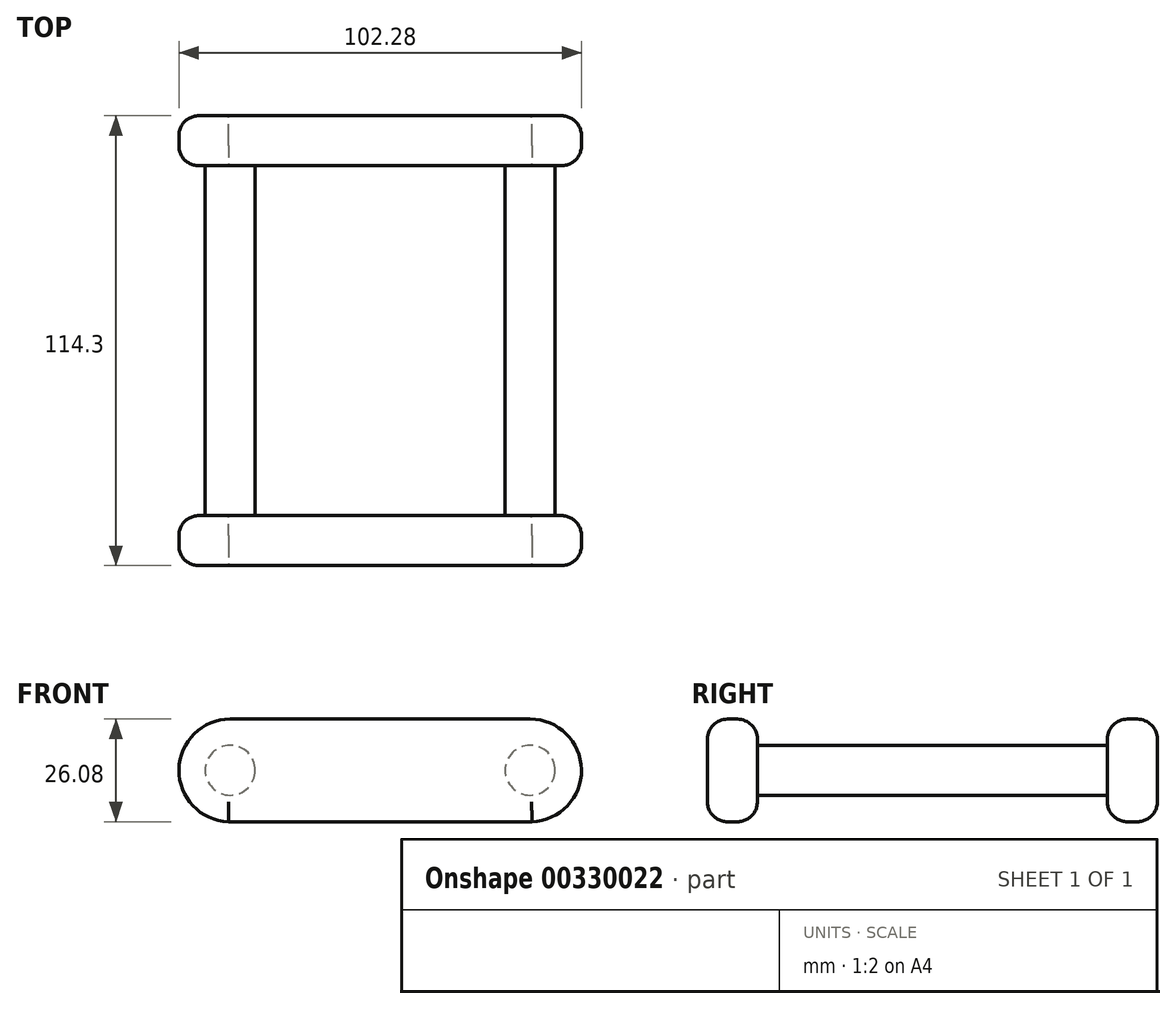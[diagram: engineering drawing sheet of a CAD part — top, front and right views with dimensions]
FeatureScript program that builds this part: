
annotation { "Feature Type Name" : "Feature", "Feature Type Description" : "" }
export const myFeature = defineFeature(function(context is Context, id is Id, definition is map)
    precondition{}
    {
        {
            var Q0;
            Q0=qCreatedBy(makeId("Front.planeOp"),FACE);
            var sketch = newSketch(context, id + "F0", { "sketchPlane" : qUnion([Q0])});
            skCircle(sketch, "E0", {"center": v(-38.1, 0) * mm, "radius": 6.35 * mm});
            skCircle(sketch, "E1", {"center": v(38.1, 0) * mm, "radius": 6.35 * mm});
            skSolve(sketch);
        }
        {
            var Q0;
            Q0 = qSketchRegion(id + "F0", true);
            extrude(context, id + "F1", {"entities" : qUnion([Q0]), "depth" : 50.8 * mm, "hasSecondDirection" : true, "secondDirectionOppositeDirection" : true, "secondDirectionDepth" : 50.8 * mm});
        }
        {
            var Q0;
            Q0=qCreatedBy(makeId("Front.planeOp"),FACE);
            cPlane(context, id + "F2", {"entities" : qUnion([Q0]), "cplaneType" : CPlaneType.OFFSET, "offset" : 50.8 * mm, "width" : 152.4 * mm, "height" : 152.4 * mm});
        }
        {
            var Q0;
            Q0=qCreatedBy(id+"F2.planeOp",FACE);
            var sketch = newSketch(context, id + "F3", { "sketchPlane" : qUnion([Q0])});
            skArc(sketch, "E2", {"start": v(-38.1, 12.99) * mm, "mid": v(-51.14, 0.18) * mm, "end": v(-38.57, -13.09) * mm});
            skLineSegment(sketch, "E3", {"start": v(-38.1, 12.99) * mm, "end": v(0, 12.99) * mm});
            skLineSegment(sketch, "E4", {"start": v(-38.57, -13.09) * mm, "end": v(0, -13.09) * mm});
            skLineSegment(sketch, "E5.MirrorCS", {"start": v(38.1, 12.99) * mm, "end": v(0, 12.99) * mm});
            skLineSegment(sketch, "E6.MirrorCS", {"start": v(38.57, -13.09) * mm, "end": v(0, -13.09) * mm});
            skArc(sketch, "E7.MirrorCS", {"start": v(38.1, 12.99) * mm, "mid": v(51.14, 0.18) * mm, "end": v(38.57, -13.09) * mm});
            skSolve(sketch);
        }
        {
            var Q0;
            Q0=makeQuery(id+"F3.imprint","IMPRINT",FACE,{"disambiguationData":[TD([[makeQuery(id+"F3.imprint","IMPRINT",EDGE,{"derivedFrom":sQuery(id+"F3.wireOp",EDGE,"E2")}),1.0]])]});
            var Q1;
            Q1=sQuery(id+"F3.wireOp",EDGE,"E2");
            var Q2;
            Q2=sQuery(id+"F3.wireOp",EDGE,"E3");
            var Q3;
            Q3=sQuery(id+"F3.wireOp",EDGE,"E4");
            var Q4;
            Q4=sQuery(id+"F3.wireOp",EDGE,"E5.MirrorCS");
            var Q5;
            Q5=sQuery(id+"F3.wireOp",EDGE,"E6.MirrorCS");
            var Q6;
            Q6=sQuery(id+"F3.wireOp",EDGE,"E7.MirrorCS");
            extrude(context, id + "F4", {"entities" : qUnion([Q0]), "operationType" : NewBodyOperationType.ADD, "surfaceEntities" : qUnion([Q1, Q2, Q3, Q4, Q5, Q6]), "oppositeDirection" : true, "depth" : 6.35 * mm, "hasSecondDirection" : true, "secondDirectionOppositeDirection" : false, "secondDirectionDepth" : 6.35 * mm});
        }
        {
            var Q0;
            Q0=qCreatedBy(makeId("Front.planeOp"),FACE);
            cPlane(context, id + "F5", {"entities" : qUnion([Q0]), "cplaneType" : CPlaneType.OFFSET, "offset" : 50.8 * mm, "oppositeDirection" : true, "width" : 152.4 * mm, "height" : 152.4 * mm});
        }
        {
            var Q0;
            Q0=qCreatedBy(id+"F5.planeOp",FACE);
            var sketch = newSketch(context, id + "F6", { "sketchPlane" : qUnion([Q0])});
            skArc(sketch, "E8", {"start": v(-38.1, 12.99) * mm, "mid": v(-51.14, 0.18) * mm, "end": v(-38.57, -13.09) * mm});
            skLineSegment(sketch, "E9", {"start": v(-38.1, 12.99) * mm, "end": v(0, 12.99) * mm});
            skLineSegment(sketch, "E10", {"start": v(-38.57, -13.09) * mm, "end": v(0, -13.09) * mm});
            skLineSegment(sketch, "E11.MirrorCS", {"start": v(38.1, 12.99) * mm, "end": v(0, 12.99) * mm});
            skLineSegment(sketch, "E12.MirrorCS", {"start": v(38.57, -13.09) * mm, "end": v(0, -13.09) * mm});
            skArc(sketch, "E13.MirrorCS", {"start": v(38.1, 12.99) * mm, "mid": v(51.14, 0.18) * mm, "end": v(38.57, -13.09) * mm});
            skSolve(sketch);
        }
        {
            var Q0;
            Q0=makeQuery(id+"F6.imprint","IMPRINT",FACE,{"disambiguationData":[TD([[makeQuery(id+"F6.imprint","IMPRINT",EDGE,{"derivedFrom":sQuery(id+"F6.wireOp",EDGE,"E8")}),1.0]])]});
            var Q1;
            Q1=sQuery(id+"F6.wireOp",EDGE,"E8");
            var Q2;
            Q2=sQuery(id+"F6.wireOp",EDGE,"E9");
            var Q3;
            Q3=sQuery(id+"F6.wireOp",EDGE,"E10");
            var Q4;
            Q4=sQuery(id+"F6.wireOp",EDGE,"E11.MirrorCS");
            var Q5;
            Q5=sQuery(id+"F6.wireOp",EDGE,"E12.MirrorCS");
            var Q6;
            Q6=sQuery(id+"F6.wireOp",EDGE,"E13.MirrorCS");
            extrude(context, id + "F7", {"entities" : qUnion([Q0]), "operationType" : NewBodyOperationType.ADD, "surfaceEntities" : qUnion([Q1, Q2, Q3, Q4, Q5, Q6]), "depth" : 6.35 * mm, "hasSecondDirection" : true, "secondDirectionOppositeDirection" : true, "secondDirectionDepth" : 6.35 * mm});
        }
        {
            var Q0;
            Q0=makeQuery(id+"F4.opExtrude","CAP_EDGE",EDGE,{"disambiguationData":[OSD([sQuery(id+"F3.wireOp",EDGE,"E3"),sQuery(id+"F3.wireOp",EDGE,"E5.MirrorCS")])],"isStart":false});
            var Q1;
            Q1=makeQuery(id+"F4.opExtrude","CAP_EDGE",EDGE,{"disambiguationData":[OSD([sQuery(id+"F3.wireOp",EDGE,"E3"),sQuery(id+"F3.wireOp",EDGE,"E5.MirrorCS")])],"isStart":true});
            var Q2;
            Q2=makeQuery(id+"F4.opExtrude","CAP_EDGE",EDGE,{"disambiguationData":[OSD([sQuery(id+"F3.wireOp",EDGE,"E7.MirrorCS")])],"isStart":true});
            var Q3;
            Q3=makeQuery(id+"F4.opExtrude","CAP_EDGE",EDGE,{"disambiguationData":[OSD([sQuery(id+"F3.wireOp",EDGE,"E4"),sQuery(id+"F3.wireOp",EDGE,"E6.MirrorCS")])],"isStart":true});
            var Q4;
            Q4=makeQuery(id+"F4.opExtrude","CAP_EDGE",EDGE,{"disambiguationData":[OSD([sQuery(id+"F3.wireOp",EDGE,"E4"),sQuery(id+"F3.wireOp",EDGE,"E6.MirrorCS")])],"isStart":false});
            var Q5;
            Q5=makeQuery(id+"F7.opExtrude","CAP_EDGE",EDGE,{"disambiguationData":[OSD([sQuery(id+"F6.wireOp",EDGE,"E10"),sQuery(id+"F6.wireOp",EDGE,"E12.MirrorCS")])],"isStart":false});
            var Q6;
            Q6=makeQuery(id+"F7.opExtrude","CAP_EDGE",EDGE,{"disambiguationData":[OSD([sQuery(id+"F6.wireOp",EDGE,"E10"),sQuery(id+"F6.wireOp",EDGE,"E12.MirrorCS")])],"isStart":true});
            var Q7;
            Q7=makeQuery(id+"F7.opExtrude","CAP_EDGE",EDGE,{"disambiguationData":[OSD([sQuery(id+"F6.wireOp",EDGE,"E9"),sQuery(id+"F6.wireOp",EDGE,"E11.MirrorCS")])],"isStart":false});
            var Q8;
            Q8=makeQuery(id+"F7.opExtrude","CAP_EDGE",EDGE,{"disambiguationData":[OSD([sQuery(id+"F6.wireOp",EDGE,"E9"),sQuery(id+"F6.wireOp",EDGE,"E11.MirrorCS")])],"isStart":true});
            var Q9;
            Q9=makeQuery(id+"F7.opExtrude","CAP_EDGE",EDGE,{"disambiguationData":[OSD([sQuery(id+"F6.wireOp",EDGE,"E13.MirrorCS")])],"isStart":true});
            fillet(context, id + "F8", {"entities" : qUnion([Q0, Q1, Q2, Q3, Q4, Q5, Q6, Q7, Q8, Q9]), "radius" : 5.08 * mm, "tangentPropagation" : true, "allowEdgeOverflow" : false});
        }
    });
